# Revit family: CARNEGIE_BAFFLES_RIPPLE
name_source: partatom
category: Generic Models
revit_build: Autodesk Revit 2015 (Build: 20160512_1515(x64)
units: mm (PartAtom-declared; Revit-internal decimal feet)

## types (12) — shared parameters

## per-type parameters (varying)
| type | BAFFLE TYPE |
| CARNEGIE_BAFFLE_RIPPLE F_ROD | CARNEGIE_BAFFLE_RIPPLE F |
| CARNEGIE_BAFFEL_RIPPLE E_ROD | CARNEGIE_BAFFLE_RIPPLE E |
| CARNEGIE_BAFFEL_RIPPLE D_ROD | CARNEGIE_BAFFLE_RIPPLE D |
| CARNEGIE_BAFFEL_RIPPLE C_ROD | CARNEGIE_BAFFLE_RIPPLE C |
| CARNEGIE_BAFFEL_RIPPLE B_ROD | CARNEGIE_BAFFLE_RIPPLE B |
| CARNEGIE_BAFFLE_RIPPLE A_ROD | CARNEGIE_BAFFLE_RIPPLE A |
| CARNEGIE_BAFFLE_RIPPLE A_CABLE | CARNEGIE_BAFFLE_RIPPLE A_CABLE |
| CARNEGIE_BAFFLE_RIPPLE B_CABLE | CARNEGIE_BAFFLE_RIPPLE B_CABLE |
| CARNEGIE_BAFFLE_RIPPLE C_CABLE | CARNEGIE_BAFFLE_RIPPLE C_CABLE |
| CARNEGIE_BAFFLE_RIPPLE D_CABLE | CARNEGIE_BAFFLE_RIPPLE D_CABLE |
| CARNEGIE_BAFFLE_RIPPLE E_CABLE | CARNEGIE_BAFFLE_RIPPLE E_CABLE |
| CARNEGIE_BAFFLE_RIPPLE F_CABLE | CARNEGIE_BAFFLE_RIPPLE F_CABLE |

## geometry (parser evidence)
native form markers: Sweep x38
no freeform markers — native parametric forms only
